# Revit family: BISLEY_CC_Filing_Cabinets
name_source: partatom
category: Furniture
revit_build: Autodesk Revit 2018 (Build: 20180423_1000(x64)
units: mm (PartAtom-declared; Revit-internal decimal feet)

## family parameters
Always vertical = Yes
Cut with Voids When Loaded = No
OmniClass Number = 23.40.20.00
OmniClass Title = General Furniture and Specialties
Room Calculation Point = No
Shared = No
Work Plane-Based = No

## types (3) — shared parameters
Category = Furniture
Compliance Standards Certification = BS EN 14074 2004, BS EN 14073 Part 2 & 3 2004
Depth = 622 mm  [stored 2.04068 ft]
Drawer width1 = 213 mm  [stored 0.698819 ft]
Drawer width2 = -213 mm  [stored -0.698819 ft]
Finish = Powder Coated
Label position = 135 mm
Manufacturer = BISLEY
Material = Steel
Model = CC Filing Cabinet
Range = Contract Filing Cabinets
Routine Maintenance = We recommend you clean your unit with warm water and a mild detergent solution. A damp cloth can be used to remove dust particles.
URL = www.bisley.com
Uniclass 2015 Code = PR_40_30_29
Uniclass2015Title = Shelves and Storage Units
Uniclass2015Version = V1.1
Warranty = 5 years from date of purchase
Width = 470 mm  [stored 1.54199 ft]
plinth height = 70 mm  [stored 0.229659 ft]

## per-type parameters (varying)
| type | Description | Dimensions | Height | Model Reference | Number of drawers | Product Information | Weight |
| CC2H1A | 2 Drawer Cabinet | 711 x 470 x 622 mm | 711 mm | CC2H1A | 2 | 2 Drawer Cabinet | 22.19kg |
| CC3H1A | 3 Drawer Filing Cabinet | 1016 x 470 x 622 mm | 1016 mm | CC3H1A | 3 | 3 Drawer Filing Cabinet | 30.73kg |
| CC4H1A | 4 Drawer Cabinet | 1321 x 470 x 622 mm | 1321 mm  [stored 4.33399 ft] | CC2H1A | 4 | 4 Drawer Cabinet | 39.18kg |

note: [stored X ft] marks values corroborated as IEEE doubles in the binary element streams (Revit-internal decimal feet)

## geometry (parser evidence)
native form markers: Sweep x2
no freeform markers — native parametric forms only
